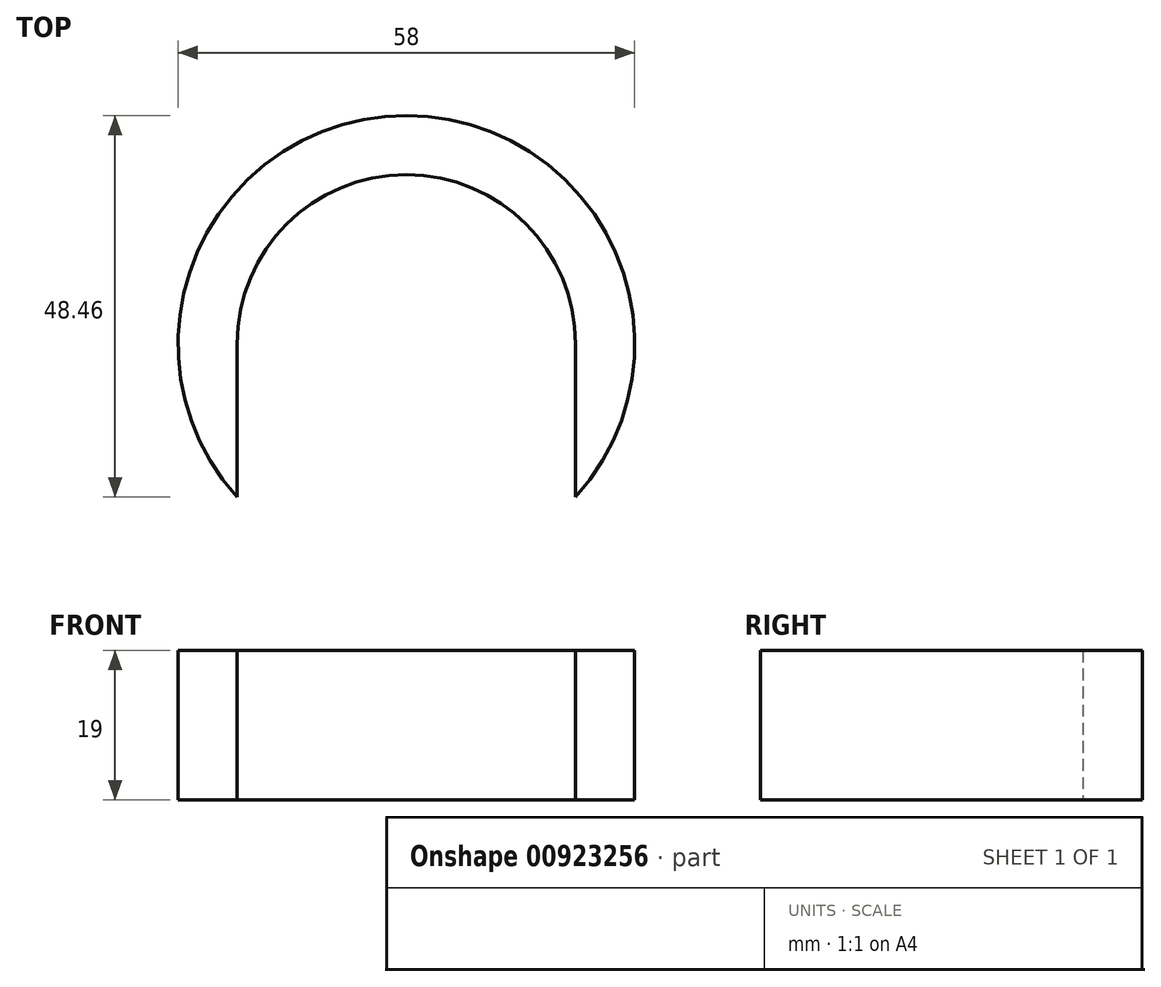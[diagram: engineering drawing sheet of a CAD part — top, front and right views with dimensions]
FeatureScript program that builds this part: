
annotation { "Feature Type Name" : "Feature", "Feature Type Description" : "" }
export const myFeature = defineFeature(function(context is Context, id is Id, definition is map)
    precondition{}
    {
        {
            var Q0;
            Q0=qCreatedBy(makeId("Top.planeOp"),FACE);
            var sketch = newSketch(context, id + "F0", { "sketchPlane" : qUnion([Q0])});
            skCircle(sketch, "E0", {"center": v(0, 0) * mm, "radius": 29 * mm});
            skCircle(sketch, "E1", {"center": v(0, 0) * mm, "radius": 21.5 * mm});
            skLineSegment(sketch, "E2", {"start": v(-21.5, 0) * mm, "end": v(-21.5, -19.46) * mm});
            skLineSegment(sketch, "E3", {"start": v(21.5, 0) * mm, "end": v(21.5, -19.46) * mm});
            skSolve(sketch);
        }
        {
            var Q0;
            {var subQ0=sQuery(id+"F0.wireOp",EDGE,"E2");Q0=makeQuery(id+"F0.imprint","IMPRINT",FACE,{"disambiguationData":[TD([[makeQuery(id+"F0.imprint","IMPRINT",EDGE,{"derivedFrom":subQ0}),-1.0]])]});}
            extrude(context, id + "F1", {"entities" : qUnion([Q0]), "depth" : 19 * mm, "offsetDistance" : 25 * mm});
        }
    });
